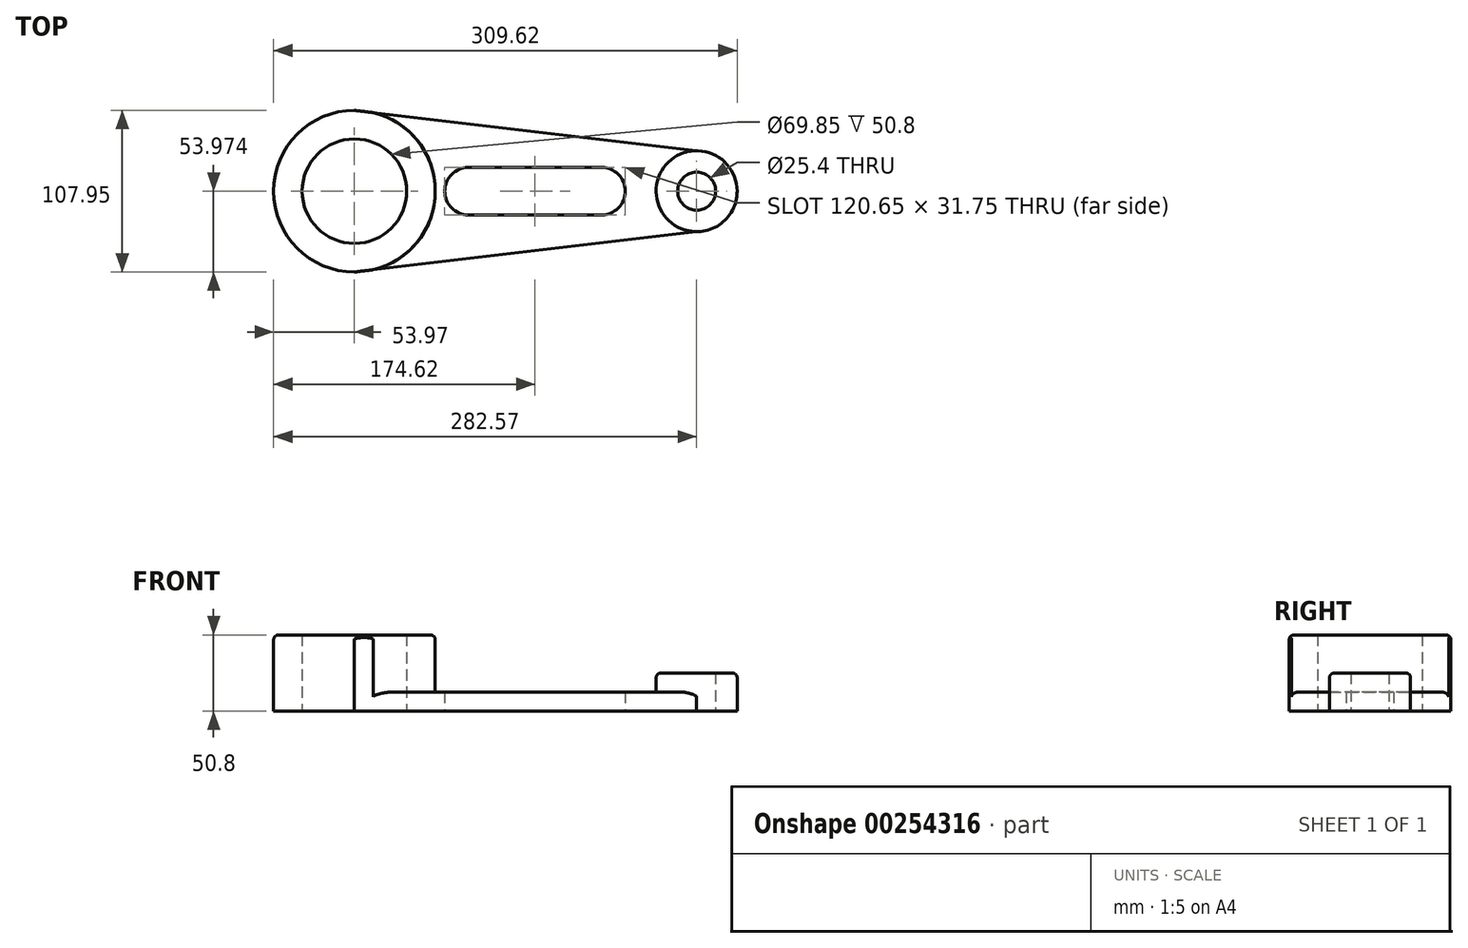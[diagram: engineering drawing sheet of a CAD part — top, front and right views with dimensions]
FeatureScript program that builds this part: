
annotation { "Feature Type Name" : "Feature", "Feature Type Description" : "" }
export const myFeature = defineFeature(function(context is Context, id is Id, definition is map)
    precondition{}
    {
        {
            var Q0;
            Q0=qCreatedBy(makeId("Top.planeOp"),FACE);
            var sketch = newSketch(context, id + "F0", { "sketchPlane" : qUnion([Q0])});
            skCircle(sketch, "E0", {"center": v(-41.8, -13.84) * mm, "radius": 53.98 * mm});
            skCircle(sketch, "E1", {"center": v(-41.8, -13.84) * mm, "radius": 34.93 * mm});
            skLineSegment(sketch, "E2", {"start": v(-41.8, -13.84) * mm, "end": v(186.8, -13.84) * mm});
            skCircle(sketch, "E3", {"center": v(186.8, -13.84) * mm, "radius": 27.05 * mm});
            skCircle(sketch, "E4", {"center": v(186.8, -13.84) * mm, "radius": 12.7 * mm});
            skLineSegment(sketch, "E5", {"start": v(-41.8, -13.84) * mm, "end": v(34.4, -13.84) * mm});
            skArc(sketch, "E6", {"start": v(34.4, 2.04) * mm, "mid": v(18.52, -13.84) * mm, "end": v(34.4, -29.71) * mm});
            skLineSegment(sketch, "E7", {"start": v(34.4, -13.84) * mm, "end": v(123.3, -13.84) * mm});
            skArc(sketch, "E8", {"start": v(123.3, -29.71) * mm, "mid": v(139.17, -13.84) * mm, "end": v(123.3, 2.04) * mm});
            skLineSegment(sketch, "E9", {"start": v(34.4, -29.71) * mm, "end": v(123.3, -29.71) * mm});
            skLineSegment(sketch, "E10", {"start": v(34.4, 2.04) * mm, "end": v(123.3, 2.04) * mm});
            skPoint(sketch, "E11", {"position": v(186.8, 13.21) * mm});
            skPoint(sketch, "E12", {"position": v(-41.8, 40.14) * mm});
            skPoint(sketch, "E13", {"position": v(-41.8, -67.81) * mm});
            skPoint(sketch, "E14", {"position": v(186.8, -40.89) * mm});
            skLineSegment(sketch, "E15", {"start": v(-41.8, 40.14) * mm, "end": v(186.8, 13.21) * mm});
            skLineSegment(sketch, "E16", {"start": v(-41.8, -67.81) * mm, "end": v(186.8, -40.89) * mm});
            skSolve(sketch);
        }
        {
            var Q0;
            {var subQ0=sQuery(id+"F0.wireOp",EDGE,"E15");var subQ1=sQuery(id+"F0.wireOp",EDGE,"E0");var subQ2=makeQuery(id+"F0.imprint","INTERSECT",VERTEX,{"disambiguationData":[OD(0.0)],"derivedFrom":[subQ1,subQ0]});Q0=makeQuery(id+"F0.imprint","IMPRINT",FACE,{"disambiguationData":[TD([[makeQuery(id+"F0.imprint","IMPRINT",EDGE,{"disambiguationData":[TD([[subQ2,1.0]])],"derivedFrom":subQ1}),1.0]])]});}
            var Q1;
            {var subQ0=sQuery(id+"F0.wireOp",EDGE,"E16");var subQ1=sQuery(id+"F0.wireOp",EDGE,"E0");var subQ2=makeQuery(id+"F0.imprint","INTERSECT",VERTEX,{"disambiguationData":[OD(0.0)],"derivedFrom":[subQ1,subQ0]});Q1=makeQuery(id+"F0.imprint","IMPRINT",FACE,{"disambiguationData":[TD([[makeQuery(id+"F0.imprint","IMPRINT",EDGE,{"disambiguationData":[TD([[subQ2,-1.0]])],"derivedFrom":subQ1}),1.0]])]});}
            var Q2;
            Q2=makeQuery(id+"F0.imprint","IMPRINT",FACE,{"disambiguationData":[TD([[makeQuery(id+"F0.imprint","IMPRINT",EDGE,{"derivedFrom":sQuery(id+"F0.wireOp",EDGE,"E1")}),-1.0]])]});
            extrude(context, id + "F1", {"entities" : qUnion([Q0, Q1, Q2]), "depth" : 50.8 * mm});
        }
        {
            var Q0;
            {var subQ10=sQuery(id+"F0.wireOp",EDGE,"E10");Q0=makeQuery(id+"F0.imprint","IMPRINT",FACE,{"disambiguationData":[TD([[makeQuery(id+"F0.imprint","IMPRINT",EDGE,{"derivedFrom":subQ10}),1.0]])]});}
            var Q1;
            {var subQ5=sQuery(id+"F0.wireOp",EDGE,"E9");Q1=makeQuery(id+"F0.imprint","IMPRINT",FACE,{"disambiguationData":[TD([[makeQuery(id+"F0.imprint","IMPRINT",EDGE,{"derivedFrom":subQ5}),-1.0]])]});}
            extrude(context, id + "F2", {"entities" : qUnion([Q0, Q1]), "operationType" : NewBodyOperationType.ADD, "depth" : 12.7 * mm});
        }
        {
            var Q0;
            Q0=makeQuery(id+"F0.imprint","IMPRINT",FACE,{"disambiguationData":[TD([[makeQuery(id+"F0.imprint","IMPRINT",EDGE,{"derivedFrom":sQuery(id+"F0.wireOp",EDGE,"E4")}),-1.0]])]});
            extrude(context, id + "F3", {"entities" : qUnion([Q0]), "operationType" : NewBodyOperationType.ADD, "depth" : 25.4 * mm});
        }
        {
            var Q0;
            Q0=makeQuery(id+"F2.opExtrude","CAP_EDGE",EDGE,{"disambiguationData":[OSD([sQuery(id+"F0.wireOp",EDGE,"E0")])],"isStart":false});
            var Q1;
            Q1=makeQuery(id+"F2.opExtrude","CAP_EDGE",EDGE,{"disambiguationData":[OSD([sQuery(id+"F0.wireOp",EDGE,"E3")])],"isStart":false});
            var Q2;
            Q2=makeQuery(id+"F2.opExtrude","CAP_EDGE",EDGE,{"disambiguationData":[OSD([sQuery(id+"F0.wireOp",EDGE,"E16")])],"isStart":false});
            var Q3;
            Q3=makeQuery(id+"F2.opExtrude","CAP_EDGE",EDGE,{"disambiguationData":[OSD([sQuery(id+"F0.wireOp",EDGE,"E15")])],"isStart":false});
            var Q4;
            Q4=makeQuery(id+"F1.opExtrude","CAP_EDGE",EDGE,{"disambiguationData":[OSD([sQuery(id+"F0.wireOp",EDGE,"E0")])],"isStart":false});
            var Q5;
            Q5=makeQuery(id+"F3.opExtrude","CAP_EDGE",EDGE,{"disambiguationData":[OSD([sQuery(id+"F0.wireOp",EDGE,"E3")])],"isStart":false});
            fillet(context, id + "F4", {"entities" : qUnion([Q0, Q1, Q2, Q3, Q4, Q5]), "radius" : 3.17 * mm, "tangentPropagation" : true, "allowEdgeOverflow" : false});
        }
    });
